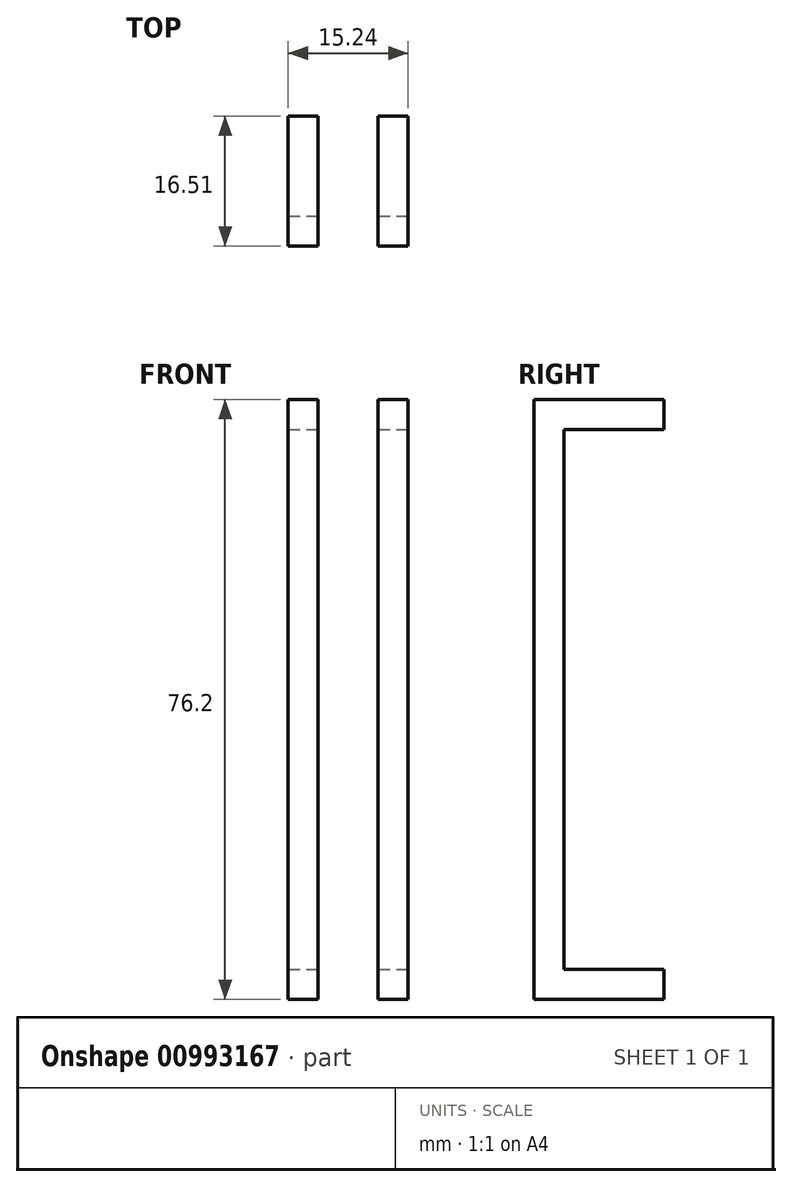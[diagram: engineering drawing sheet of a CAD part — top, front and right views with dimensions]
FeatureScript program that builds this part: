
annotation { "Feature Type Name" : "Feature", "Feature Type Description" : "" }
export const myFeature = defineFeature(function(context is Context, id is Id, definition is map)
    precondition{}
    {
        {
            var Q0;
            Q0=qCreatedBy(makeId("Front.planeOp"),FACE);
            var sketch = newSketch(context, id + "F0", { "sketchPlane" : qUnion([Q0])});
            skLineSegment(sketch, "E0.bottom", {"start": v(-53.55, 85.88) * mm, "end": v(-38.3, 85.88) * mm});
            skLineSegment(sketch, "E0.top", {"start": v(-53.55, 9.68) * mm, "end": v(-38.3, 9.68) * mm});
            skLineSegment(sketch, "E0.left", {"start": v(-53.55, 85.88) * mm, "end": v(-53.55, 9.68) * mm});
            skLineSegment(sketch, "E0.right", {"start": v(-38.3, 85.88) * mm, "end": v(-38.3, 9.68) * mm});
            skLineSegment(sketch, "E1.bottom", {"start": v(-49.74, 85.88) * mm, "end": v(-42.12, 85.88) * mm});
            skLineSegment(sketch, "E1.top", {"start": v(-49.74, 9.68) * mm, "end": v(-42.12, 9.68) * mm});
            skLineSegment(sketch, "E1.left", {"start": v(-49.74, 85.88) * mm, "end": v(-49.74, 9.68) * mm});
            skLineSegment(sketch, "E1.right", {"start": v(-42.12, 85.88) * mm, "end": v(-42.12, 9.68) * mm});
            skLineSegment(sketch, "E2.bottom", {"start": v(-53.55, 82.07) * mm, "end": v(-38.3, 82.07) * mm});
            skLineSegment(sketch, "E2.top", {"start": v(-53.55, 13.49) * mm, "end": v(-38.3, 13.49) * mm});
            skLineSegment(sketch, "E2.left", {"start": v(-53.55, 82.07) * mm, "end": v(-53.55, 13.49) * mm});
            skLineSegment(sketch, "E2.right", {"start": v(-38.3, 82.07) * mm, "end": v(-38.3, 13.49) * mm});
            skSolve(sketch);
        }
        {
            var Q0;
            {var subQ0=sQuery(id+"F0.wireOp",EDGE,"E0.left");var subQ1=sQuery(id+"F0.wireOp",EDGE,"E0.bottom");var subQ2=makeQuery(id+"F0.imprint","INTERSECT",VERTEX,{"derivedFrom":[subQ1,subQ0]});Q0=makeQuery(id+"F0.imprint","IMPRINT",FACE,{"disambiguationData":[TD([[makeQuery(id+"F0.imprint","IMPRINT",EDGE,{"disambiguationData":[TD([[subQ2,-1.0]])],"derivedFrom":subQ1}),-1.0]])]});}
            var Q1;
            {var subQ0=sQuery(id+"F0.wireOp",EDGE,"E1.bottom");Q1=makeQuery(id+"F0.imprint","IMPRINT",FACE,{"disambiguationData":[TD([[makeQuery(id+"F0.imprint","IMPRINT",EDGE,{"derivedFrom":subQ0}),-1.0]])]});}
            var Q2;
            {var subQ0=sQuery(id+"F0.wireOp",EDGE,"E0.right");var subQ1=sQuery(id+"F0.wireOp",EDGE,"E0.bottom");var subQ2=makeQuery(id+"F0.imprint","INTERSECT",VERTEX,{"derivedFrom":[subQ1,subQ0]});Q2=makeQuery(id+"F0.imprint","IMPRINT",FACE,{"disambiguationData":[TD([[makeQuery(id+"F0.imprint","IMPRINT",EDGE,{"disambiguationData":[TD([[subQ2,1.0]])],"derivedFrom":subQ1}),-1.0]])]});}
            var Q3;
            {var subQ5=sQuery(id+"F0.wireOp",EDGE,"E2.right");Q3=makeQuery(id+"F0.imprint","IMPRINT",FACE,{"disambiguationData":[TD([[makeQuery(id+"F0.imprint","IMPRINT",EDGE,{"derivedFrom":subQ5}),-1.0]])]});}
            var Q4;
            {var subQ5=sQuery(id+"F0.wireOp",EDGE,"E2.left");Q4=makeQuery(id+"F0.imprint","IMPRINT",FACE,{"disambiguationData":[TD([[makeQuery(id+"F0.imprint","IMPRINT",EDGE,{"derivedFrom":subQ5}),1.0]])]});}
            var Q5;
            {var subQ0=sQuery(id+"F0.wireOp",EDGE,"E0.left");var subQ1=sQuery(id+"F0.wireOp",EDGE,"E0.top");var subQ2=makeQuery(id+"F0.imprint","INTERSECT",VERTEX,{"derivedFrom":[subQ1,subQ0]});Q5=makeQuery(id+"F0.imprint","IMPRINT",FACE,{"disambiguationData":[TD([[makeQuery(id+"F0.imprint","IMPRINT",EDGE,{"disambiguationData":[TD([[subQ2,-1.0]])],"derivedFrom":subQ1}),1.0]])]});}
            var Q6;
            {var subQ0=sQuery(id+"F0.wireOp",EDGE,"E1.top");Q6=makeQuery(id+"F0.imprint","IMPRINT",FACE,{"disambiguationData":[TD([[makeQuery(id+"F0.imprint","IMPRINT",EDGE,{"derivedFrom":subQ0}),1.0]])]});}
            var Q7;
            {var subQ0=sQuery(id+"F0.wireOp",EDGE,"E0.right");var subQ1=sQuery(id+"F0.wireOp",EDGE,"E0.top");var subQ2=makeQuery(id+"F0.imprint","INTERSECT",VERTEX,{"derivedFrom":[subQ1,subQ0]});Q7=makeQuery(id+"F0.imprint","IMPRINT",FACE,{"disambiguationData":[TD([[makeQuery(id+"F0.imprint","IMPRINT",EDGE,{"disambiguationData":[TD([[subQ2,1.0]])],"derivedFrom":subQ1}),1.0]])]});}
            extrude(context, id + "F1", {"entities" : qUnion([Q0, Q1, Q2, Q3, Q4, Q5, Q6, Q7]), "depth" : 3.8 * mm, "offsetDistance" : 25.4 * mm});
        }
        {
            var Q0;
            {var subQ5=sQuery(id+"F0.wireOp",EDGE,"E2.left");Q0=makeQuery(id+"F0.imprint","IMPRINT",FACE,{"disambiguationData":[TD([[makeQuery(id+"F0.imprint","IMPRINT",EDGE,{"derivedFrom":subQ5}),1.0]])]});}
            var Q1;
            {var subQ0=sQuery(id+"F0.wireOp",EDGE,"E0.left");var subQ1=sQuery(id+"F0.wireOp",EDGE,"E0.bottom");var subQ2=makeQuery(id+"F0.imprint","INTERSECT",VERTEX,{"derivedFrom":[subQ1,subQ0]});Q1=makeQuery(id+"F0.imprint","IMPRINT",FACE,{"disambiguationData":[TD([[makeQuery(id+"F0.imprint","IMPRINT",EDGE,{"disambiguationData":[TD([[subQ2,-1.0]])],"derivedFrom":subQ1}),-1.0]])]});}
            var Q2;
            {var subQ0=sQuery(id+"F0.wireOp",EDGE,"E0.right");var subQ1=sQuery(id+"F0.wireOp",EDGE,"E0.bottom");var subQ2=makeQuery(id+"F0.imprint","INTERSECT",VERTEX,{"derivedFrom":[subQ1,subQ0]});Q2=makeQuery(id+"F0.imprint","IMPRINT",FACE,{"disambiguationData":[TD([[makeQuery(id+"F0.imprint","IMPRINT",EDGE,{"disambiguationData":[TD([[subQ2,1.0]])],"derivedFrom":subQ1}),-1.0]])]});}
            var Q3;
            {var subQ5=sQuery(id+"F0.wireOp",EDGE,"E2.right");Q3=makeQuery(id+"F0.imprint","IMPRINT",FACE,{"disambiguationData":[TD([[makeQuery(id+"F0.imprint","IMPRINT",EDGE,{"derivedFrom":subQ5}),-1.0]])]});}
            var Q4;
            {var subQ0=sQuery(id+"F0.wireOp",EDGE,"E0.right");var subQ1=sQuery(id+"F0.wireOp",EDGE,"E0.top");var subQ2=makeQuery(id+"F0.imprint","INTERSECT",VERTEX,{"derivedFrom":[subQ1,subQ0]});Q4=makeQuery(id+"F0.imprint","IMPRINT",FACE,{"disambiguationData":[TD([[makeQuery(id+"F0.imprint","IMPRINT",EDGE,{"disambiguationData":[TD([[subQ2,1.0]])],"derivedFrom":subQ1}),1.0]])]});}
            var Q5;
            {var subQ0=sQuery(id+"F0.wireOp",EDGE,"E0.left");var subQ1=sQuery(id+"F0.wireOp",EDGE,"E0.top");var subQ2=makeQuery(id+"F0.imprint","INTERSECT",VERTEX,{"derivedFrom":[subQ1,subQ0]});Q5=makeQuery(id+"F0.imprint","IMPRINT",FACE,{"disambiguationData":[TD([[makeQuery(id+"F0.imprint","IMPRINT",EDGE,{"disambiguationData":[TD([[subQ2,-1.0]])],"derivedFrom":subQ1}),1.0]])]});}
            extrude(context, id + "F2", {"entities" : qUnion([Q0, Q1, Q2, Q3, Q4, Q5]), "operationType" : NewBodyOperationType.ADD, "oppositeDirection" : true, "depth" : 1.27 * mm, "offsetDistance" : 25.4 * mm});
        }
        {
            var Q0;
            {var subQ0=sQuery(id+"F0.wireOp",EDGE,"E0.left");var subQ1=sQuery(id+"F0.wireOp",EDGE,"E0.bottom");var subQ2=makeQuery(id+"F0.imprint","INTERSECT",VERTEX,{"derivedFrom":[subQ1,subQ0]});Q0=makeQuery(id+"F0.imprint","IMPRINT",FACE,{"disambiguationData":[TD([[makeQuery(id+"F0.imprint","IMPRINT",EDGE,{"disambiguationData":[TD([[subQ2,-1.0]])],"derivedFrom":subQ1}),-1.0]])]});}
            var Q1;
            {var subQ0=sQuery(id+"F0.wireOp",EDGE,"E0.right");var subQ1=sQuery(id+"F0.wireOp",EDGE,"E0.bottom");var subQ2=makeQuery(id+"F0.imprint","INTERSECT",VERTEX,{"derivedFrom":[subQ1,subQ0]});Q1=makeQuery(id+"F0.imprint","IMPRINT",FACE,{"disambiguationData":[TD([[makeQuery(id+"F0.imprint","IMPRINT",EDGE,{"disambiguationData":[TD([[subQ2,1.0]])],"derivedFrom":subQ1}),-1.0]])]});}
            var Q2;
            {var subQ0=sQuery(id+"F0.wireOp",EDGE,"E0.left");var subQ1=sQuery(id+"F0.wireOp",EDGE,"E0.top");var subQ2=makeQuery(id+"F0.imprint","INTERSECT",VERTEX,{"derivedFrom":[subQ1,subQ0]});Q2=makeQuery(id+"F0.imprint","IMPRINT",FACE,{"disambiguationData":[TD([[makeQuery(id+"F0.imprint","IMPRINT",EDGE,{"disambiguationData":[TD([[subQ2,-1.0]])],"derivedFrom":subQ1}),1.0]])]});}
            var Q3;
            {var subQ0=sQuery(id+"F0.wireOp",EDGE,"E0.right");var subQ1=sQuery(id+"F0.wireOp",EDGE,"E0.top");var subQ2=makeQuery(id+"F0.imprint","INTERSECT",VERTEX,{"derivedFrom":[subQ1,subQ0]});Q3=makeQuery(id+"F0.imprint","IMPRINT",FACE,{"disambiguationData":[TD([[makeQuery(id+"F0.imprint","IMPRINT",EDGE,{"disambiguationData":[TD([[subQ2,1.0]])],"derivedFrom":subQ1}),1.0]])]});}
            extrude(context, id + "F3", {"entities" : qUnion([Q0, Q1, Q2, Q3]), "operationType" : NewBodyOperationType.ADD, "depth" : 15.24 * mm, "offsetDistance" : 25.4 * mm});
        }
        {
            var Q0;
            {var subQ0=sQuery(id+"F0.wireOp",EDGE,"E2.bottom");Q0=makeQuery(id+"F3.opExtrude","SWEPT_FACE",FACE,{"disambiguationData":[OSD([subQ0]),TDD([makeQuery(id+"F0.imprint","IMPRINT",EDGE,{"disambiguationData":[TD([[makeQuery(id+"F0.imprint","INTERSECT",VERTEX,{"derivedFrom":[sQuery(id+"F0.wireOp",EDGE,"E1.left"),subQ0]}),1.0]])],"derivedFrom":subQ0})])]});}
            var sketch = newSketch(context, id + "F4", { "sketchPlane" : qUnion([Q0])});
            skLineSegment(sketch, "E3", {"start": v(-53.55, 11.43) * mm, "end": v(-49.74, 11.43) * mm});
            skSolve(sketch);
        }
        {
            var Q0;
            {var subQ0=sQuery(id+"F4.wireOp",EDGE,"E3");Q0=makeQuery(id+"F4.imprint","IMPRINT",FACE,{"disambiguationData":[TD([[makeQuery(id+"F4.imprint","IMPRINT",EDGE,{"derivedFrom":subQ0}),1.0]])]});}
            extrude(context, id + "F5", {"entities" : qUnion([Q0]), "operationType" : NewBodyOperationType.ADD, "depth" : 68.58 * mm, "offsetDistance" : 25.4 * mm});
        }
        {
            var Q0;
            {var subQ0=sQuery(id+"F0.wireOp",EDGE,"E2.bottom");Q0=makeQuery(id+"F3.opExtrude","SWEPT_FACE",FACE,{"disambiguationData":[OSD([subQ0]),TDD([makeQuery(id+"F0.imprint","IMPRINT",EDGE,{"disambiguationData":[TD([[makeQuery(id+"F0.imprint","INTERSECT",VERTEX,{"derivedFrom":[sQuery(id+"F0.wireOp",EDGE,"E1.right"),subQ0]}),-1.0]])],"derivedFrom":subQ0})])]});}
            var sketch = newSketch(context, id + "F6", { "sketchPlane" : qUnion([Q0])});
            skLineSegment(sketch, "E4", {"start": v(-42.12, 11.43) * mm, "end": v(-38.3, 11.43) * mm});
            skSolve(sketch);
        }
        {
            var Q0;
            {var subQ0=sQuery(id+"F6.wireOp",EDGE,"E4");Q0=makeQuery(id+"F6.imprint","IMPRINT",FACE,{"disambiguationData":[TD([[makeQuery(id+"F6.imprint","IMPRINT",EDGE,{"derivedFrom":subQ0}),1.0]])]});}
            extrude(context, id + "F7", {"entities" : qUnion([Q0]), "operationType" : NewBodyOperationType.ADD, "depth" : 68.58 * mm, "offsetDistance" : 25.4 * mm});
        }
    });
